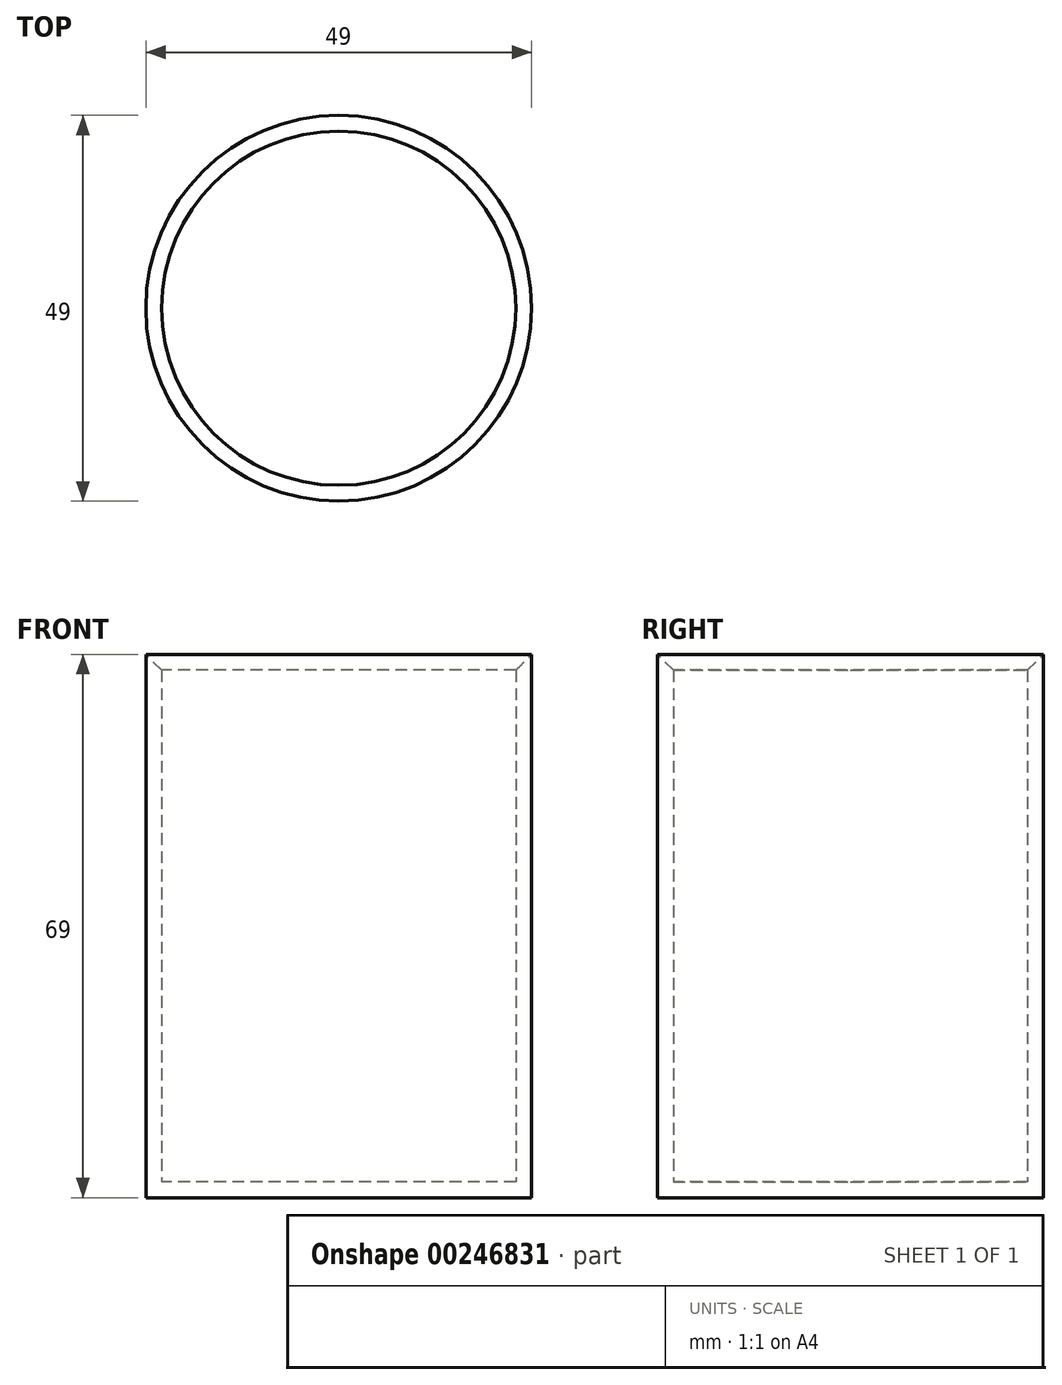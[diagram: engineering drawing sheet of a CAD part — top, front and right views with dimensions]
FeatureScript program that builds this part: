
annotation { "Feature Type Name" : "Feature", "Feature Type Description" : "" }
export const myFeature = defineFeature(function(context is Context, id is Id, definition is map)
    precondition{}
    {
        {
            var Q0;
            Q0=qCreatedBy(makeId("Top.planeOp"),FACE);
            var sketch = newSketch(context, id + "F0", { "sketchPlane" : qUnion([Q0])});
            skCircle(sketch, "E0", {"center": v(0, 0) * mm, "radius": 24.5 * mm});
            skSolve(sketch);
        }
        {
            var Q0;
            Q0=makeQuery(id+"F0.imprint","IMPRINT",FACE,{"disambiguationData":[TD([[makeQuery(id+"F0.imprint","IMPRINT",EDGE,{"derivedFrom":sQuery(id+"F0.wireOp",EDGE,"E0")}),1.0]])]});
            extrude(context, id + "F1", {"entities" : qUnion([Q0]), "depth" : (65 + 2 + 5) * mm});
        }
        {
            var Q0;
            Q0=makeQuery(id+"F1.opExtrude","CAP_FACE",FACE,{"disambiguationData":[OSD([sQuery(id+"F0.wireOp",EDGE,"E0")])],"isStart":false});
            shell(context, id + "F2", {"entities" : qUnion([Q0]), "thickness" : 2 * mm});
        }
        {
            var Q0;
            {var subQ0=sQuery(id+"F0.wireOp",EDGE,"E0");Q0=makeQuery(id+"F2.opShell","OFFSET_EDGE",EDGE,{"disambiguationData":[OSD([subQ0]),TDD([makeQuery(id+"F1.opExtrude","CAP_EDGE",EDGE,{"disambiguationData":[OSD([subQ0])],"isStart":false})])]});}
            chamfer(context, id + "F3", {"entities" : qUnion([Q0]), "width" : 5 * mm, "tangentPropagation" : true});
        }
    });
